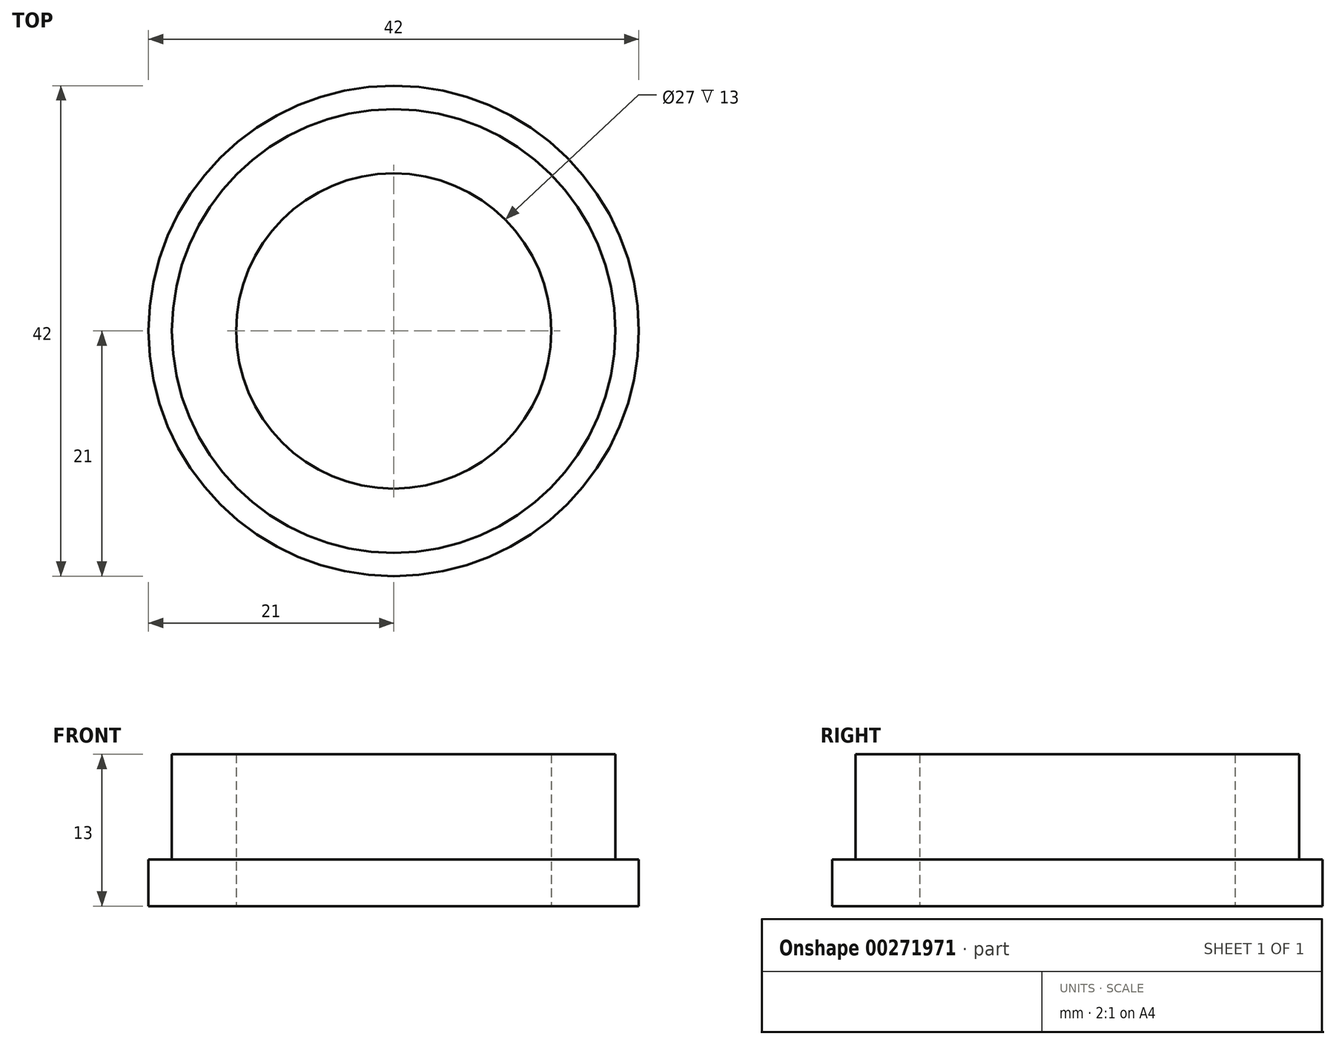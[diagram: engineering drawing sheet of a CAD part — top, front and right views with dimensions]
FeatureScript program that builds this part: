
annotation { "Feature Type Name" : "Feature", "Feature Type Description" : "" }
export const myFeature = defineFeature(function(context is Context, id is Id, definition is map)
    precondition{}
    {
        {
            var Q0;
            Q0=qCreatedBy(makeId("Front.planeOp"),FACE);
            var sketch = newSketch(context, id + "F0", { "sketchPlane" : qUnion([Q0])});
            skLineSegment(sketch, "E0", {"start": v(13.5, 0) * mm, "end": v(13.5, 13) * mm});
            skLineSegment(sketch, "E1", {"start": v(13.5, 13) * mm, "end": v(19, 13) * mm});
            skLineSegment(sketch, "E2", {"start": v(19, 13) * mm, "end": v(19, 4) * mm});
            skLineSegment(sketch, "E3", {"start": v(19, 4) * mm, "end": v(21, 4) * mm});
            skLineSegment(sketch, "E4", {"start": v(21, 4) * mm, "end": v(21, 0) * mm});
            skLineSegment(sketch, "E5", {"start": v(13.5, 0) * mm, "end": v(21, 0) * mm});
            skLineSegment(sketch, "E6", {"start": v(0, 0) * mm, "end": v(0, 13) * mm, "construction": true});
            skSolve(sketch);
        }
        {
            var Q0;
            Q0 = qSketchRegion(id + "F0", true);
            var Q1;
            Q1=sQuery(id+"F0.wireOp",EDGE,"E6");
            revolve(context, id + "F1", {"entities" : qUnion([Q0]), "axis" : qUnion([Q1]), "revolveType" : RevolveType.FULL});
        }
    });
